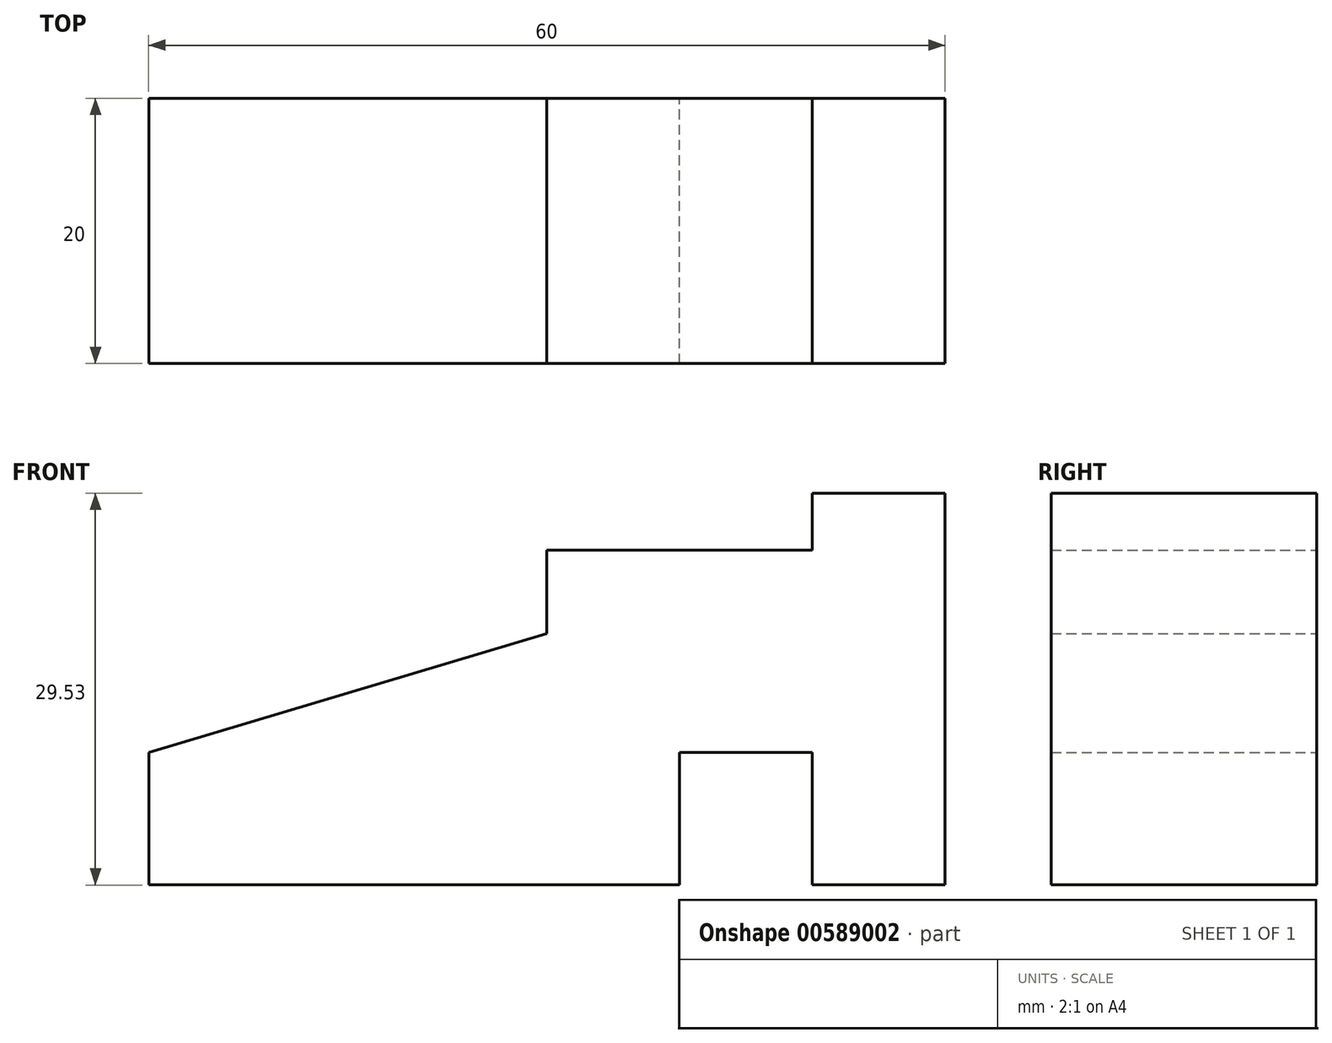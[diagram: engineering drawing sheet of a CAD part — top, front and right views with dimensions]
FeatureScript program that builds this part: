
annotation { "Feature Type Name" : "Feature", "Feature Type Description" : "" }
export const myFeature = defineFeature(function(context is Context, id is Id, definition is map)
    precondition{}
    {
        {
            var Q0;
            Q0=qCreatedBy(makeId("Front.planeOp"),FACE);
            var sketch = newSketch(context, id + "F0", { "sketchPlane" : qUnion([Q0])});
            skLineSegment(sketch, "E0", {"start": v(-27.33, -8.62) * mm, "end": v(12.67, -8.62) * mm});
            skLineSegment(sketch, "E1", {"start": v(12.67, -8.62) * mm, "end": v(12.67, 1.38) * mm});
            skLineSegment(sketch, "E2", {"start": v(12.67, 1.38) * mm, "end": v(22.67, 1.38) * mm});
            skLineSegment(sketch, "E3", {"start": v(22.67, 1.38) * mm, "end": v(22.67, -8.62) * mm});
            skLineSegment(sketch, "E4", {"start": v(22.67, -8.62) * mm, "end": v(32.67, -8.62) * mm});
            skLineSegment(sketch, "E5", {"start": v(32.67, -8.62) * mm, "end": v(32.67, 20.9) * mm});
            skLineSegment(sketch, "E6", {"start": v(32.67, 20.9) * mm, "end": v(22.67, 20.9) * mm});
            skLineSegment(sketch, "E7", {"start": v(22.67, 20.9) * mm, "end": v(22.67, 16.62) * mm});
            skLineSegment(sketch, "E8", {"start": v(22.67, 16.62) * mm, "end": v(2.67, 16.62) * mm});
            skLineSegment(sketch, "E9", {"start": v(2.67, 16.62) * mm, "end": v(2.67, 10.34) * mm});
            skLineSegment(sketch, "E10", {"start": v(-27.33, -8.62) * mm, "end": v(-27.33, 1.38) * mm});
            skLineSegment(sketch, "E11", {"start": v(-27.33, 1.38) * mm, "end": v(2.67, 10.34) * mm});
            skSolve(sketch);
        }
        {
            var Q0;
            Q0 = qSketchRegion(id + "F0", true);
            extrude(context, id + "F1", {"entities" : qUnion([Q0]), "depth" : 20 * mm, "offsetDistance" : 25 * mm});
        }
    });
